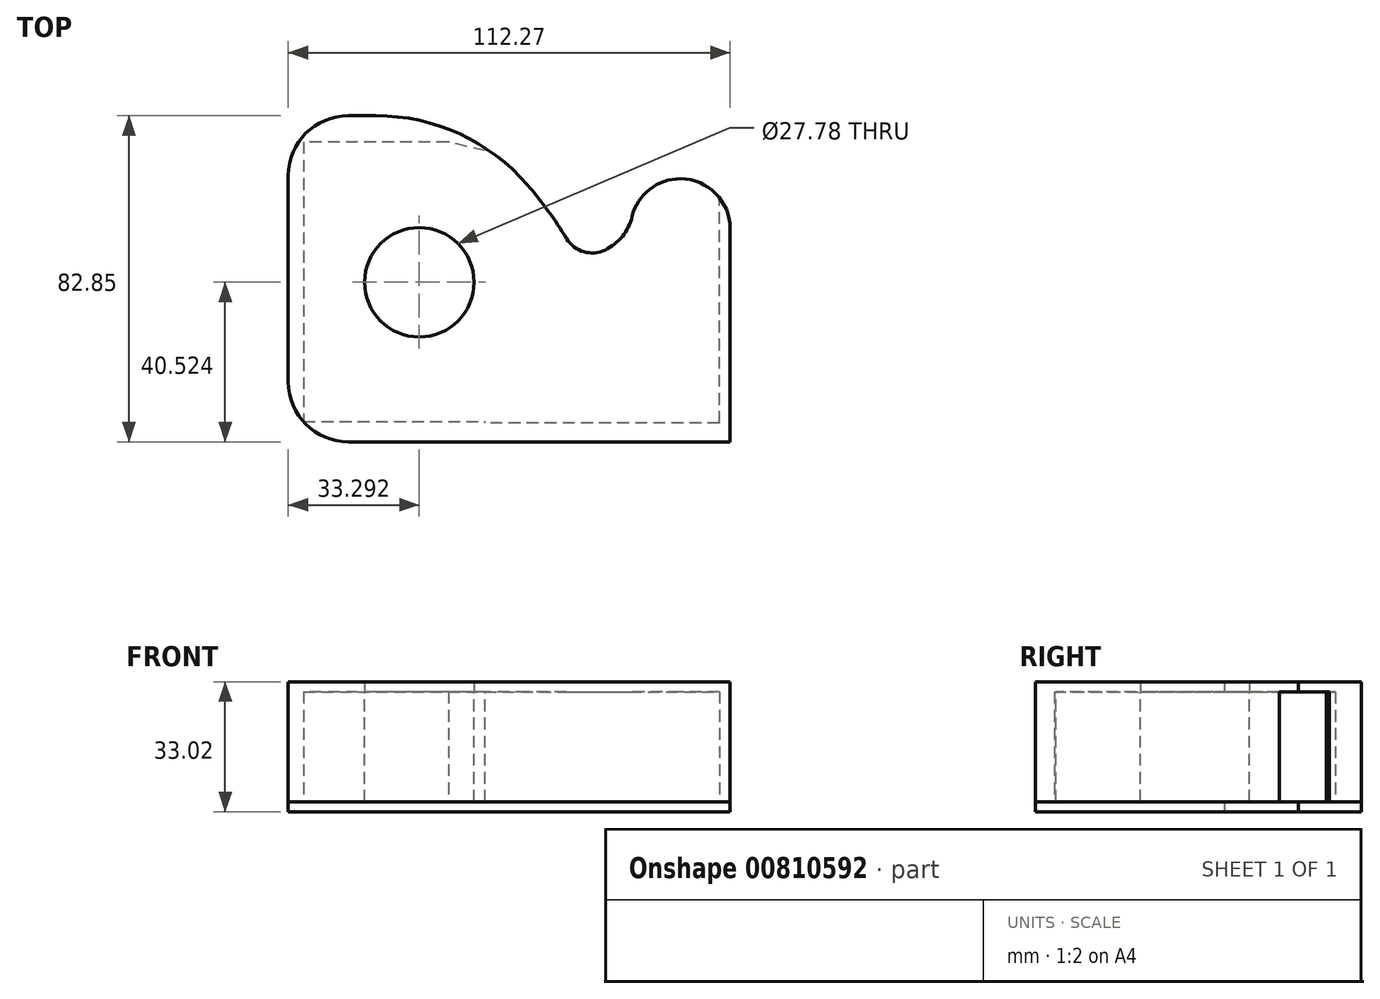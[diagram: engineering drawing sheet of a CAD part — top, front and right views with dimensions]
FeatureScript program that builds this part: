
annotation { "Feature Type Name" : "Feature", "Feature Type Description" : "" }
export const myFeature = defineFeature(function(context is Context, id is Id, definition is map)
    precondition{}
    {
        {
            var Q0;
            Q0=qCreatedBy(makeId("Top.planeOp"),FACE);
            var sketch = newSketch(context, id + "F0", { "sketchPlane" : qUnion([Q0])});
            skLineSegment(sketch, "E0", {"start": v(-43.23, -48.14) * mm, "end": v(60, -48.14) * mm});
            skLineSegment(sketch, "E1", {"start": v(60, -48.14) * mm, "end": v(60, 7.87) * mm});
            skLineSegment(sketch, "E2", {"start": v(60, 7.87) * mm, "end": v(45.55, 7.87) * mm});
            skLineSegment(sketch, "E3", {"start": v(45.55, 7.87) * mm, "end": v(45.55, -14.07) * mm});
            skLineSegment(sketch, "E4", {"start": v(45.55, -14.07) * mm, "end": v(12.52, -10.97) * mm});
            skLineSegment(sketch, "E5", {"start": v(12.52, -10.97) * mm, "end": v(19.23, 16.65) * mm});
            skLineSegment(sketch, "E6", {"start": v(19.23, 16.65) * mm, "end": v(-6.43, 22.88) * mm});
            skLineSegment(sketch, "E7", {"start": v(-6.43, 22.88) * mm, "end": v(-43.23, 22.88) * mm});
            skLineSegment(sketch, "E8", {"start": v(-43.23, 22.88) * mm, "end": v(-43.23, -48.14) * mm});
            skLineSegment(sketch, "E9", {"start": v(-47.1, 29.55) * mm, "end": v(-47.1, -53.3) * mm});
            skLineSegment(sketch, "E10", {"start": v(-47.1, -53.3) * mm, "end": v(65.17, -53.3) * mm});
            skLineSegment(sketch, "E11", {"start": v(65.17, -53.3) * mm, "end": v(65.17, 13.55) * mm});
            skLineSegment(sketch, "E12", {"start": v(65.17, 13.55) * mm, "end": v(39.88, 13.55) * mm});
            skLineSegment(sketch, "E13", {"start": v(39.88, 13.55) * mm, "end": v(39.88, -7.61) * mm});
            skLineSegment(sketch, "E14", {"start": v(39.88, -7.61) * mm, "end": v(21.3, -5.03) * mm});
            skLineSegment(sketch, "E15", {"start": v(21.3, -5.03) * mm, "end": v(27.23, 20.26) * mm});
            skLineSegment(sketch, "E16", {"start": v(27.23, 20.26) * mm, "end": v(-6.07, 29.55) * mm});
            skLineSegment(sketch, "E17", {"start": v(-6.07, 29.55) * mm, "end": v(-47.1, 29.55) * mm});
            skSolve(sketch);
        }
        {
            var Q0;
            Q0=makeQuery(id+"F0.imprint","IMPRINT",FACE,{"disambiguationData":[TD([[makeQuery(id+"F0.imprint","IMPRINT",EDGE,{"derivedFrom":sQuery(id+"F0.wireOp",EDGE,"E0")}),-1.0]])]});
            extrude(context, id + "F1", {"entities" : qUnion([Q0]), "depth" : 27.94 * mm, "offsetDistance" : 25.4 * mm});
        }
        {
            var Q0;
            Q0=makeQuery(id+"F1.opExtrude","CAP_FACE",FACE,{"disambiguationData":[OSD([sQuery(id+"F0.wireOp",EDGE,"E0"),sQuery(id+"F0.wireOp",EDGE,"E1"),sQuery(id+"F0.wireOp",EDGE,"E2"),sQuery(id+"F0.wireOp",EDGE,"E3"),sQuery(id+"F0.wireOp",EDGE,"E4"),sQuery(id+"F0.wireOp",EDGE,"E5"),sQuery(id+"F0.wireOp",EDGE,"E6"),sQuery(id+"F0.wireOp",EDGE,"E7"),sQuery(id+"F0.wireOp",EDGE,"E8"),sQuery(id+"F0.wireOp",EDGE,"E9"),sQuery(id+"F0.wireOp",EDGE,"E10"),sQuery(id+"F0.wireOp",EDGE,"E11"),sQuery(id+"F0.wireOp",EDGE,"E12"),sQuery(id+"F0.wireOp",EDGE,"E13"),sQuery(id+"F0.wireOp",EDGE,"E14"),sQuery(id+"F0.wireOp",EDGE,"E15"),sQuery(id+"F0.wireOp",EDGE,"E16"),sQuery(id+"F0.wireOp",EDGE,"E17")])],"isStart":false});
            var sketch = newSketch(context, id + "F2", { "sketchPlane" : qUnion([Q0])});
            skCircle(sketch, "E18", {"center": v(-13.8, -12.78) * mm, "radius": 13.89 * mm});
            skLineSegment(sketch, "E19", {"start": v(-47.1, 29.55) * mm, "end": v(-47.1, -53.3) * mm});
            skLineSegment(sketch, "E20", {"start": v(-47.1, -53.3) * mm, "end": v(65.17, -53.3) * mm});
            skLineSegment(sketch, "E21", {"start": v(65.17, -53.3) * mm, "end": v(65.17, 13.55) * mm});
            skLineSegment(sketch, "E22", {"start": v(65.17, 13.55) * mm, "end": v(39.88, 13.55) * mm});
            skLineSegment(sketch, "E23", {"start": v(39.88, 13.55) * mm, "end": v(39.88, -7.61) * mm});
            skLineSegment(sketch, "E24", {"start": v(39.88, -7.61) * mm, "end": v(21.3, -5.03) * mm});
            skLineSegment(sketch, "E25", {"start": v(21.3, -5.03) * mm, "end": v(27.23, 20.26) * mm});
            skLineSegment(sketch, "E26", {"start": v(27.23, 20.26) * mm, "end": v(-6.07, 29.55) * mm});
            skLineSegment(sketch, "E27", {"start": v(-6.07, 29.55) * mm, "end": v(-47.1, 29.55) * mm});
            skSolve(sketch);
        }
        {
            var Q0;
            Q0=makeQuery(id+"F2.imprint","IMPRINT",FACE,{"disambiguationData":[TD([[makeQuery(id+"F2.imprint","IMPRINT",EDGE,{"derivedFrom":sQuery(id+"F2.wireOp",EDGE,"E19")}),1.0]])]});
            var Q1;
            Q1=makeQuery(id+"F2.imprint","IMPRINT",FACE,{"disambiguationData":[TD([[makeQuery(id+"F2.imprint","IMPRINT",EDGE,{"derivedFrom":sQuery(id+"F2.wireOp",EDGE,"E18")}),-1.0]])]});
            extrude(context, id + "F3", {"entities" : qUnion([Q0, Q1]), "operationType" : NewBodyOperationType.ADD, "depth" : 2.54 * mm, "offsetDistance" : 25.4 * mm});
        }
        {
            var Q0;
            Q0=makeQuery(id+"F2.imprint","IMPRINT",FACE,{"disambiguationData":[TD([[makeQuery(id+"F2.imprint","IMPRINT",EDGE,{"derivedFrom":sQuery(id+"F2.wireOp",EDGE,"E18")}),1.0]])]});
            extrude(context, id + "F4", {"entities" : qUnion([Q0]), "oppositeDirection" : true, "depth" : 27.94 * mm, "offsetDistance" : 25.4 * mm});
        }
        {
            var Q0;
            Q0=makeQuery(id+"F1.opExtrude","CAP_FACE",FACE,{"disambiguationData":[OSD([sQuery(id+"F0.wireOp",EDGE,"E0"),sQuery(id+"F0.wireOp",EDGE,"E1"),sQuery(id+"F0.wireOp",EDGE,"E2"),sQuery(id+"F0.wireOp",EDGE,"E3"),sQuery(id+"F0.wireOp",EDGE,"E4"),sQuery(id+"F0.wireOp",EDGE,"E5"),sQuery(id+"F0.wireOp",EDGE,"E6"),sQuery(id+"F0.wireOp",EDGE,"E7"),sQuery(id+"F0.wireOp",EDGE,"E8"),sQuery(id+"F0.wireOp",EDGE,"E9"),sQuery(id+"F0.wireOp",EDGE,"E10"),sQuery(id+"F0.wireOp",EDGE,"E11"),sQuery(id+"F0.wireOp",EDGE,"E12"),sQuery(id+"F0.wireOp",EDGE,"E13"),sQuery(id+"F0.wireOp",EDGE,"E14"),sQuery(id+"F0.wireOp",EDGE,"E15"),sQuery(id+"F0.wireOp",EDGE,"E16"),sQuery(id+"F0.wireOp",EDGE,"E17")])],"isStart":true});
            var sketch = newSketch(context, id + "F5", { "sketchPlane" : qUnion([Q0])});
            skLineSegment(sketch, "E28", {"start": v(-6.07, -29.55) * mm, "end": v(-47.1, -29.55) * mm});
            skLineSegment(sketch, "E29", {"start": v(-47.1, -29.55) * mm, "end": v(-47.1, 53.3) * mm});
            skLineSegment(sketch, "E30", {"start": v(-47.1, 53.3) * mm, "end": v(65.17, 53.3) * mm});
            skLineSegment(sketch, "E31", {"start": v(65.17, 53.3) * mm, "end": v(65.17, -13.55) * mm});
            skLineSegment(sketch, "E32", {"start": v(65.17, -13.55) * mm, "end": v(39.88, -13.55) * mm});
            skLineSegment(sketch, "E33", {"start": v(39.88, -13.55) * mm, "end": v(39.88, 7.61) * mm});
            skLineSegment(sketch, "E34", {"start": v(39.88, 7.61) * mm, "end": v(21.3, 5.03) * mm});
            skLineSegment(sketch, "E35", {"start": v(21.3, 5.03) * mm, "end": v(27.23, -20.26) * mm});
            skLineSegment(sketch, "E36", {"start": v(27.23, -20.26) * mm, "end": v(-6.07, -29.55) * mm});
            skSolve(sketch);
        }
        {
            var Q0;
            Q0=makeQuery(id+"F5.imprint","IMPRINT",FACE,{"disambiguationData":[TD([[makeQuery(id+"F5.imprint","IMPRINT",EDGE,{"derivedFrom":sQuery(id+"F5.wireOp",EDGE,"E28")}),-1.0]])]});
            var Q1;
            Q1=makeQuery(id+"F5.imprint","IMPRINT",FACE,{"disambiguationData":[TD([[makeQuery(id+"F5.imprint","IMPRINT",EDGE,{"derivedFrom":makeQuery(id+"F1.opExtrude","CAP_EDGE",EDGE,{"disambiguationData":[OSD([sQuery(id+"F0.wireOp",EDGE,"E0")])],"isStart":true})}),-1.0]])]});
            extrude(context, id + "F6", {"entities" : qUnion([Q0, Q1]), "depth" : 2.54 * mm, "offsetDistance" : 25.4 * mm});
        }
        {
            var Q0;
            Q0=makeQuery(id+"F4.opExtrude","CAP_FACE",FACE,{"disambiguationData":[OSD([sQuery(id+"F2.wireOp",EDGE,"E18")])],"isStart":true});
            extrude(context, id + "F7", {"entities" : qUnion([Q0]), "depth" : 2.54 * mm, "offsetDistance" : 25.4 * mm});
        }
        {
            var Q0;
            Q0=qCreatedBy(makeId("Front.planeOp"),FACE);
            cPlane(context, id + "F8", {"entities" : qUnion([Q0]), "cplaneType" : CPlaneType.OFFSET, "offset" : 44.96 * mm, "oppositeDirection" : true, "width" : 152.4 * mm, "height" : 152.4 * mm});
        }
        {
            var Q0;
            Q0=qCreatedBy(id+"F8.planeOp",FACE);
            var sketch = newSketch(context, id + "F9", { "sketchPlane" : qUnion([Q0])});
            skLineSegment(sketch, "E37", {"start": v(2.85, 0) * mm, "end": v(2.85, 27.94) * mm});
            skLineSegment(sketch, "E38", {"start": v(2.85, 27.94) * mm, "end": v(62.47, 27.94) * mm});
            skLineSegment(sketch, "E39", {"start": v(62.47, 27.94) * mm, "end": v(62.47, 0) * mm});
            skLineSegment(sketch, "E40", {"start": v(62.47, 0) * mm, "end": v(2.85, 0) * mm});
            skSolve(sketch);
        }
        {
            var Q0;
            Q0 = qSketchRegion(id + "F9", true);
            extrude(context, id + "F10", {"entities" : qUnion([Q0]), "operationType" : NewBodyOperationType.REMOVE, "depth" : 93.47 * mm, "offsetDistance" : 25.4 * mm});
        }
        {
            var Q0;
            Q0=makeQuery(id+"F3.boolean.opBoolean","MERGE",EDGE,{"derivedFrom":[makeQuery(id+"F1.opExtrude","SWEPT_EDGE",EDGE,{"disambiguationData":[OSD([sQuery(id+"F0.wireOp",EDGE,"E12"),sQuery(id+"F0.wireOp",EDGE,"E13")])]}),makeQuery(id+"F3.opExtrude","SWEPT_EDGE",EDGE,{"disambiguationData":[OSD([sQuery(id+"F2.wireOp",EDGE,"E22"),sQuery(id+"F2.wireOp",EDGE,"E23")])]})]});
            var Q1;
            Q1=makeQuery(id+"F6.opExtrude","SWEPT_EDGE",EDGE,{"disambiguationData":[OSD([sQuery(id+"F5.wireOp",EDGE,"E32"),sQuery(id+"F5.wireOp",EDGE,"E33")])]});
            fillet(context, id + "F11", {"entities" : qUnion([Q0, Q1]), "radius" : 12.7 * mm, "tangentPropagation" : true, "allowEdgeOverflow" : false});
        }
        {
            var Q0;
            Q0=makeQuery(id+"F3.boolean.opBoolean","MERGE",EDGE,{"derivedFrom":[makeQuery(id+"F1.opExtrude","SWEPT_EDGE",EDGE,{"disambiguationData":[OSD([sQuery(id+"F0.wireOp",EDGE,"E11"),sQuery(id+"F0.wireOp",EDGE,"E12")])]}),makeQuery(id+"F3.opExtrude","SWEPT_EDGE",EDGE,{"disambiguationData":[OSD([sQuery(id+"F2.wireOp",EDGE,"E21"),sQuery(id+"F2.wireOp",EDGE,"E22")])]})]});
            var Q1;
            Q1=makeQuery(id+"F6.opExtrude","SWEPT_EDGE",EDGE,{"disambiguationData":[OSD([sQuery(id+"F5.wireOp",EDGE,"E31"),sQuery(id+"F5.wireOp",EDGE,"E32")])]});
            fillet(context, id + "F12", {"entities" : qUnion([Q0, Q1]), "radius" : 12.7 * mm, "tangentPropagation" : true, "allowEdgeOverflow" : false});
        }
        {
            var Q0;
            Q0=makeQuery(id+"F3.boolean.opBoolean","MERGE",EDGE,{"derivedFrom":[makeQuery(id+"F1.opExtrude","SWEPT_EDGE",EDGE,{"disambiguationData":[OSD([sQuery(id+"F0.wireOp",EDGE,"E13"),sQuery(id+"F0.wireOp",EDGE,"E14")])]}),makeQuery(id+"F3.opExtrude","SWEPT_EDGE",EDGE,{"disambiguationData":[OSD([sQuery(id+"F2.wireOp",EDGE,"E23"),sQuery(id+"F2.wireOp",EDGE,"E24")])]})]});
            var Q1;
            Q1=makeQuery(id+"F6.opExtrude","SWEPT_EDGE",EDGE,{"disambiguationData":[OSD([sQuery(id+"F5.wireOp",EDGE,"E33"),sQuery(id+"F5.wireOp",EDGE,"E34")])]});
            fillet(context, id + "F13", {"entities" : qUnion([Q0, Q1]), "radius" : 12.7 * mm, "tangentPropagation" : true, "allowEdgeOverflow" : false});
        }
        {
            var Q0;
            Q0=makeQuery(id+"F6.opExtrude","SWEPT_EDGE",EDGE,{"disambiguationData":[OSD([sQuery(id+"F5.wireOp",EDGE,"E34"),sQuery(id+"F5.wireOp",EDGE,"E35")])]});
            var Q1;
            Q1=makeQuery(id+"F3.boolean.opBoolean","MERGE",EDGE,{"derivedFrom":[makeQuery(id+"F1.opExtrude","SWEPT_EDGE",EDGE,{"disambiguationData":[OSD([sQuery(id+"F0.wireOp",EDGE,"E14"),sQuery(id+"F0.wireOp",EDGE,"E15")])]}),makeQuery(id+"F3.opExtrude","SWEPT_EDGE",EDGE,{"disambiguationData":[OSD([sQuery(id+"F2.wireOp",EDGE,"E24"),sQuery(id+"F2.wireOp",EDGE,"E25")])]})]});
            fillet(context, id + "F14", {"entities" : qUnion([Q0, Q1]), "radius" : 12.7 * mm, "tangentPropagation" : true, "allowEdgeOverflow" : false});
        }
        {
            var Q0;
            Q0=makeQuery(id+"F3.boolean.opBoolean","MERGE",EDGE,{"derivedFrom":[makeQuery(id+"F1.opExtrude","SWEPT_EDGE",EDGE,{"disambiguationData":[OSD([sQuery(id+"F0.wireOp",EDGE,"E15"),sQuery(id+"F0.wireOp",EDGE,"E16")])]}),makeQuery(id+"F3.opExtrude","SWEPT_EDGE",EDGE,{"disambiguationData":[OSD([sQuery(id+"F2.wireOp",EDGE,"E25"),sQuery(id+"F2.wireOp",EDGE,"E26")])]})]});
            var Q1;
            Q1=makeQuery(id+"F6.opExtrude","SWEPT_EDGE",EDGE,{"disambiguationData":[OSD([sQuery(id+"F5.wireOp",EDGE,"E35"),sQuery(id+"F5.wireOp",EDGE,"E36")])]});
            fillet(context, id + "F15", {"entities" : qUnion([Q0, Q1]), "radius" : 101.6 * mm, "tangentPropagation" : true, "allowEdgeOverflow" : false});
        }
        {
            var Q0;
            Q0=makeQuery(id+"F15.opFillet","BLEND_EDGE",EDGE,{"blendedFrom":[makeQuery(id+"F3.boolean.opBoolean","MERGE",EDGE,{"derivedFrom":[makeQuery(id+"F1.opExtrude","SWEPT_EDGE",EDGE,{"disambiguationData":[OSD([sQuery(id+"F0.wireOp",EDGE,"E15"),sQuery(id+"F0.wireOp",EDGE,"E16")])]}),makeQuery(id+"F3.opExtrude","SWEPT_EDGE",EDGE,{"disambiguationData":[OSD([sQuery(id+"F2.wireOp",EDGE,"E25"),sQuery(id+"F2.wireOp",EDGE,"E26")])]})]}),makeQuery(id+"F3.boolean.opBoolean","MERGE",FACE,{"derivedFrom":[makeQuery(id+"F1.opExtrude","SWEPT_FACE",FACE,{"disambiguationData":[OSD([sQuery(id+"F0.wireOp",EDGE,"E17")])]}),makeQuery(id+"F3.opExtrude","SWEPT_FACE",FACE,{"disambiguationData":[OSD([sQuery(id+"F2.wireOp",EDGE,"E27")])]})]})],"blendedInto":[makeQuery(id+"F3.boolean.opBoolean","MERGE",FACE,{"derivedFrom":[makeQuery(id+"F1.opExtrude","SWEPT_FACE",FACE,{"disambiguationData":[OSD([sQuery(id+"F0.wireOp",EDGE,"E17")])]}),makeQuery(id+"F3.opExtrude","SWEPT_FACE",FACE,{"disambiguationData":[OSD([sQuery(id+"F2.wireOp",EDGE,"E27")])]})]})]});
            var Q1;
            Q1=makeQuery(id+"F15.opFillet","BLEND_EDGE",EDGE,{"blendedFrom":[makeQuery(id+"F6.opExtrude","SWEPT_EDGE",EDGE,{"disambiguationData":[OSD([sQuery(id+"F5.wireOp",EDGE,"E35"),sQuery(id+"F5.wireOp",EDGE,"E36")])]}),makeQuery(id+"F6.opExtrude","SWEPT_FACE",FACE,{"disambiguationData":[OSD([sQuery(id+"F5.wireOp",EDGE,"E28")])]})],"blendedInto":[makeQuery(id+"F6.opExtrude","SWEPT_FACE",FACE,{"disambiguationData":[OSD([sQuery(id+"F5.wireOp",EDGE,"E28")])]})]});
            fillet(context, id + "F16", {"entities" : qUnion([Q0, Q1]), "radius" : 50.8 * mm, "tangentPropagation" : true, "allowEdgeOverflow" : false});
        }
        {
            var Q0;
            {var subQ0=sQuery(id+"F2.wireOp",EDGE,"E24");var subQ1=sQuery(id+"F0.wireOp",EDGE,"E14");Q0=makeQuery(id+"F14.opFillet","BLEND_EDGE",EDGE,{"blendedFrom":[makeQuery(id+"F3.boolean.opBoolean","MERGE",EDGE,{"derivedFrom":[makeQuery(id+"F1.opExtrude","SWEPT_EDGE",EDGE,{"disambiguationData":[OSD([subQ1,sQuery(id+"F0.wireOp",EDGE,"E15")])]}),makeQuery(id+"F3.opExtrude","SWEPT_EDGE",EDGE,{"disambiguationData":[OSD([subQ0,sQuery(id+"F2.wireOp",EDGE,"E25")])]})]}),makeQuery(id+"F13.opFillet","BLEND_FACE",FACE,{"disambiguationData":[OSD([sQuery(id+"F0.wireOp",EDGE,"E13"),subQ1,sQuery(id+"F2.wireOp",EDGE,"E23"),subQ0])]})],"blendedInto":[makeQuery(id+"F13.opFillet","BLEND_FACE",FACE,{"disambiguationData":[OSD([sQuery(id+"F0.wireOp",EDGE,"E13"),subQ1,sQuery(id+"F2.wireOp",EDGE,"E23"),subQ0])]})]});}
            var Q1;
            {var subQ0=sQuery(id+"F5.wireOp",EDGE,"E34");Q1=makeQuery(id+"F14.opFillet","BLEND_EDGE",EDGE,{"blendedFrom":[makeQuery(id+"F6.opExtrude","SWEPT_EDGE",EDGE,{"disambiguationData":[OSD([subQ0,sQuery(id+"F5.wireOp",EDGE,"E35")])]}),makeQuery(id+"F13.opFillet","BLEND_FACE",FACE,{"disambiguationData":[OSD([sQuery(id+"F5.wireOp",EDGE,"E33"),subQ0])]})],"blendedInto":[makeQuery(id+"F13.opFillet","BLEND_FACE",FACE,{"disambiguationData":[OSD([sQuery(id+"F5.wireOp",EDGE,"E33"),subQ0])]})]});}
            fillet(context, id + "F17", {"entities" : qUnion([Q0, Q1]), "radius" : 7.62 * mm, "tangentPropagation" : true, "allowEdgeOverflow" : false});
        }
        {
            var Q0;
            Q0=makeQuery(id+"F3.boolean.opBoolean","MERGE",EDGE,{"derivedFrom":[makeQuery(id+"F1.opExtrude","SWEPT_EDGE",EDGE,{"disambiguationData":[OSD([sQuery(id+"F0.wireOp",EDGE,"E9"),sQuery(id+"F0.wireOp",EDGE,"E17")])]}),makeQuery(id+"F3.opExtrude","SWEPT_EDGE",EDGE,{"disambiguationData":[OSD([sQuery(id+"F2.wireOp",EDGE,"E19"),sQuery(id+"F2.wireOp",EDGE,"E27")])]})]});
            var Q1;
            Q1=makeQuery(id+"F6.opExtrude","SWEPT_EDGE",EDGE,{"disambiguationData":[OSD([sQuery(id+"F5.wireOp",EDGE,"E28"),sQuery(id+"F5.wireOp",EDGE,"E29")])]});
            fillet(context, id + "F18", {"entities" : qUnion([Q0, Q1]), "radius" : 15.24 * mm, "tangentPropagation" : true, "allowEdgeOverflow" : false});
        }
        {
            var Q0;
            Q0=makeQuery(id+"F3.boolean.opBoolean","MERGE",EDGE,{"derivedFrom":[makeQuery(id+"F1.opExtrude","SWEPT_EDGE",EDGE,{"disambiguationData":[OSD([sQuery(id+"F0.wireOp",EDGE,"E9"),sQuery(id+"F0.wireOp",EDGE,"E10")])]}),makeQuery(id+"F3.opExtrude","SWEPT_EDGE",EDGE,{"disambiguationData":[OSD([sQuery(id+"F2.wireOp",EDGE,"E19"),sQuery(id+"F2.wireOp",EDGE,"E20")])]})]});
            var Q1;
            Q1=makeQuery(id+"F6.opExtrude","SWEPT_EDGE",EDGE,{"disambiguationData":[OSD([sQuery(id+"F5.wireOp",EDGE,"E29"),sQuery(id+"F5.wireOp",EDGE,"E30")])]});
            fillet(context, id + "F19", {"entities" : qUnion([Q0, Q1]), "radius" : 15.24 * mm, "tangentPropagation" : true, "allowEdgeOverflow" : false});
        }
    });
